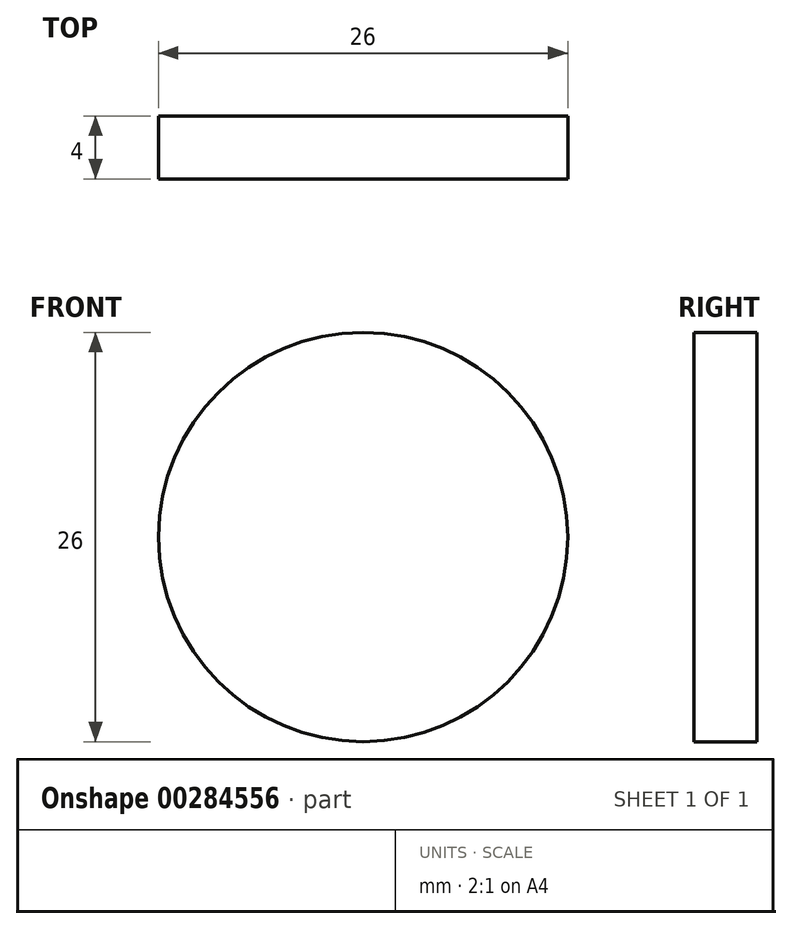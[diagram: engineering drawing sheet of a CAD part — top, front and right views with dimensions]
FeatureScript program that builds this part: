
annotation { "Feature Type Name" : "Feature", "Feature Type Description" : "" }
export const myFeature = defineFeature(function(context is Context, id is Id, definition is map)
    precondition{}
    {
        {
            var Q0;
            Q0=qCreatedBy(makeId("Front.planeOp"),FACE);
            var sketch = newSketch(context, id + "F0", { "sketchPlane" : qUnion([Q0])});
            skCircle(sketch, "E0", {"center": v(0, 0) * mm, "radius": 13 * mm});
            skSolve(sketch);
        }
        {
            var Q0;
            Q0=makeQuery(id+"F0.imprint","IMPRINT",FACE,{"disambiguationData":[TD([[makeQuery(id+"F0.imprint","IMPRINT",EDGE,{"derivedFrom":sQuery(id+"F0.wireOp",EDGE,"E0")}),1.0]])]});
            extrude(context, id + "F1", {"entities" : qUnion([Q0]), "depth" : 4 * mm});
        }
    });
